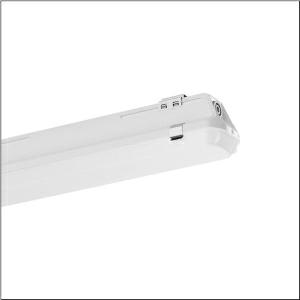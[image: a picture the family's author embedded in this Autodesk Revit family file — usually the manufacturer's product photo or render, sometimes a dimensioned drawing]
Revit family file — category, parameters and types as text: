
# Revit family: monsun_r__11_51fp109p440h_ab1f
name_source: partatom
category: Lighting Fixtures
units: mm (PartAtom-declared; Revit-internal decimal feet)

## family parameters
Cut with Voids When Loaded = No
Host = Face
Light Source = No
Part Type = Normal
Room Calculation Point = No
Round Connector Dimension = Use Diameter
Shared = No

## types (1)
- Monsun® 11 (1 x LED, 4120 lm, 22.9 W, 4000K)
    Apparent Load = 23 VA
    CIE Flux Codes = 47 77 93 94 100
    Color Rendering = 80
    Color Temperature = 4000K
    Default Elevation = 1800 mm
    Description = Monsun® 11, damp-proof luminaire, chain hanger, primary optical cover: enclosure, of PMMA, light emission: direct distribution, primary light characteristic: symmetric, installation type: suspended mounting, surface-mounted, horizontal mounting, vertical mounting, LED, rated luminous flux: 4.120lm, luminous efficacy: 180lm/W, light colour: 840, colour temperature: 4000K, control gear: ECG, with terminal, 3-pole, max. 2.5mm², mains connection: 220..240V, AC, 50/60Hz, start of lifetime: 23W, end of service life: 25W, luminaire housing, of glass-fibre reinforced polyester, uncoated, bright grey, incl. chain hanger, length: 1.590mm, width: 90mm, height: 88mm, clip for enclosure, of stainless steel (V2A), ceiling mounting element, of stainless steel (V2A), chain hanger, of stainless steel (V2A), protection rating (complete): IP66, insulation class (complete): insulation class I (protective earthing), certification: CE, ENEC, VDE, UKCA, protection symbol: D, impact resistance: IK04, permissible operating ambient temperature: -35..+40°C, standard: EN 50419, EN 60598-2-1, no direct snow, no direct sun, no direct rain, for indoor or canopied outdoor use, corresponds to IFS (International Featured Standards) requirements for safety and quality in the food industry, contact your sales advisor before using the luminaires in applications with unclear chemical exposure, large temperature fluctuations or condensation-forming humidity, LABS conformity tested according to VDMA 24364:2018-05, packaging unit: 1 piece
    Height = 89 mm
    Lamp = 1 x LED
    Lamp Light Flux = 4120 lm
    Lamp Power = 22.9 W
    Lamp count = 1
    Length = 1590 mm
    Luminous efficacy = 180 lm/W
    Manufacturer = Siteco
    ModVariant = No
    Model = 51FP109P440H
    Mounting Place = Ceiling
    Mounting Type = Surface mounted
    Number of Poles = 1
    OnlyDefault = Yes
    Power Factor = 1
    Product Name = Monsun® 11
    Product group = damp-proof luminaire
    ProductGroupID = 301
    Protection Class = Protection class I
    Protection Degree = IP 66
    RLX_Detail_Level = 1
    RLX_Emergency_Light_Flux = 0 lm
    RLX_Emergency_Type = 0
    RLX_Emergency_Type_DB = No
    RlxData = <blob elided: 88641 chars, md5=b531c348>
    Socket = socket
    Standby Power = 0 W
    System Light Flux = 4120 lm
    System Power = 23 W
    Type Comments = Product without accessories
    Type Image = l_1004748.jpg
    URL = http://relux.com
    VarID = ---
    Voltage = 0 V
    Weight = 0.00 kg
    Width = 90 mm

## geometry (parser evidence)
native form markers: Blend x4, Sweep x14
no freeform markers — native parametric forms only
